# Revit family: MSUi
name_source: partatom
category: Lighting Fixtures
units: mm (PartAtom-declared; Revit-internal decimal feet)

## family parameters
Always vertical = Yes
Cut with Voids When Loaded = No
Host = Ceiling
Light Source = Yes
Maintain Annotation Orientation = No
OmniClass Number = 23.80.70.11.14.17
OmniClass Title = Direct/Indirect
Part Type = Normal
Room Calculation Point = No
Round Connector Dimension = Use Diameter
Shared = No

## types (21) — shared parameters
Assembly Code = D5020200
Default Elevation = 0' - 0"
Description = LED Recessed Medical Surgical with Inset Door Frame
Dimming Lamp Color Temperature Shift = <None>
Emit Shape Visible in Rendering = No
Housing Finish = Metal - Viscor - White
Lamp = LED
Lens Finish = Acrylic - Viscor - Frosted Prismatic P12
Manufacturer = CERTOLUX by VISCOR
Model = MSUi
Tilt Angle = 90.00°
URL = https://www.viscor.com
Voltage = 120 V

## per-type parameters (varying)
| type | Apparent Load | Color Filter | Emit from Rectangle Length | Emit from Rectangle Width | Lamp Wattage | Length | Lens Finish Green | Photometric Web File | Width |
| MSUi-1X4-LED840K035LUNV | 32 VA | 16777215 | 3' - 11 3/4" | 0' - 11 3/4" | 32 VA | 3' - 11 3/4" | Default | MSUi-1X4-LED840K035LUNV.ies | 0' - 11 3/4" |
| MSUi-2X2-LED840K035LUNV | 31 VA | 16777215 | 1' - 11 3/4" | 1' - 11 3/4" | 31 VA | 1' - 11 3/4" | Default | MSUi-2X2-LED840K035LUNV.ies | 1' - 11 3/4" |
| MSUi-2X4-LED840K055LUNV | 45 VA | 16777215 | 3' - 11 3/4" | 1' - 11 3/4" | 45 VA | 3' - 11 3/4" | Default | MSUi-2X4-LED840K055LUNV.ies | 1' - 11 3/4" |
| MSUi-1X4-LED840K055LUNV | 51 VA | 16777215 | 3' - 11 3/4" | 0' - 11 3/4" | 51 VA | 3' - 11 3/4" | Default | MSUi-1X4-LED840K055LUNV.ies | 0' - 11 3/4" |
| MSUi-1X4-LED840K070LUNV | 68 VA | 16777215 | 3' - 11 3/4" | 0' - 11 3/4" | 68 VA | 3' - 11 3/4" | Default | MSUi-1X4-LED840K070LUNV.ies | 0' - 11 3/4" |
| MSUi-1X4-LED840K100LUNV | 96 VA | 16777215 | 3' - 11 3/4" | 0' - 11 3/4" | 96 VA | 3' - 11 3/4" | Default | MSUi-1X4-LED840K100LUNV.ies | 0' - 11 3/4" |
| MSUi-2X2-LED840K055LUNV | 50 VA | 16777215 | 1' - 11 3/4" | 1' - 11 3/4" | 50 VA | 1' - 11 3/4" | Default | MSUi-2X2-LED840K055LUNV.ies | 1' - 11 3/4" |
| MSUi-2X2-LED840K070LUNV | 65 VA | 16777215 | 1' - 11 3/4" | 1' - 11 3/4" | 65 VA | 1' - 11 3/4" | Default | MSUi-2X2-LED840K070LUNV.ies | 1' - 11 3/4" |
| MSUi-2X2-LED840K100LUNV | 93 VA | 16777215 | 1' - 11 3/4" | 1' - 11 3/4" | 93 VA | 1' - 11 3/4" | Default | MSUi-2X2-LED840K100LUNV.ies | 1' - 11 3/4" |
| MSUi-2X4-LED840K070LUNV | 59 VA | 16777215 | 3' - 11 3/4" | 1' - 11 3/4" | 59 VA | 3' - 11 3/4" | <By Category> | MSUi-2X4-LED840K070LUNV.ies | 1' - 11 3/4" |
| MSUi-2X4-LED840K100LUNV | 80 VA | 16777215 | 3' - 11 3/4" | 1' - 11 3/4" | 80 VA | 3' - 11 3/4" | <By Category> | MSUi-2X4-LED840K100LUNV.ies | 1' - 11 3/4" |
| MSUi-2X4-LED840K120LUNV | 99 VA | 16777215 | 3' - 11 3/4" | 1' - 11 3/4" | 99 VA | 3' - 11 3/4" | <By Category> | MSUi-2X4-LED840K120LUNV.ies | 1' - 11 3/4" |
| MSUi-2X4-LED840K180LUNV | 143 VA | 16777215 | 3' - 11 3/4" | 1' - 11 3/4" | 143 VA | 3' - 11 3/4" | <By Category> | MSUi-2X4-LED840K180LUNV.ies | 1' - 11 3/4" |
| MSUi-2X4-LED840K240LUNV | 198 VA | 16777215 | 3' - 11 3/4" | 1' - 11 3/4" | 198 VA | 3' - 11 3/4" | <By Category> | MSUi-2X4-LED840K240LUNV.ies | 1' - 11 3/4" |
| MSUi-1X4-LED840KxxL_32GUNV | 51 VA | 8454016 | 3' - 11 3/4" | 0' - 11 3/4" | 51 VA | 3' - 11 3/4" | Acrylic - Viscor - Frosted Prismatic P12 Green | MSUi-1X4-LED840KxxL_32GUNV.ies | 0' - 11 3/4" |
| MSUi-1X4-LED840KxxL_50GUNV | 80 VA | 8454016 | 3' - 11 3/4" | 0' - 11 3/4" | 80 VA | 3' - 11 3/4" | Acrylic - Viscor - Frosted Prismatic P12 Green | MSUi-1X4-LED840KxxL_50GUNV.ies | 0' - 11 3/4" |
| MSUi-2X2-LED840KxxL_32GUNV | 51 VA | 8454016 | 1' - 11 3/4" | 1' - 11 3/4" | 51 VA | 1' - 11 3/4" | Acrylic - Viscor - Frosted Prismatic P12 Green | MSUi-2X2-LED840KxxL_32GUNV.ies | 1' - 11 3/4" |
| MSUi-2X2-LED840KxxL_50GUNV | 50 VA | 8454016 | 1' - 11 3/4" | 1' - 11 3/4" | 50 VA | 1' - 11 3/4" | Acrylic - Viscor - Frosted Prismatic P12 Green | MSUi-2X2-LED840KxxL_50GUNV.ies | 1' - 11 3/4" |
| MSUi-2X4-LED840KxxL_32GUNV | 45 VA | 8454016 | 3' - 11 3/4" | 1' - 11 3/4" | 45 VA | 3' - 11 3/4" | Acrylic - Viscor - Frosted Prismatic P12 Green | MSUi-2X4-LED840KxxL_32GUNV.ies | 1' - 11 3/4" |
| MSUi-2X4-LED840KxxL_50GUNV | 70 VA | 8454016 | 3' - 11 3/4" | 1' - 11 3/4" | 70 VA | 3' - 11 3/4" | Acrylic - Viscor - Frosted Prismatic P12 Green | MSUi-2X4-LED840KxxL_50GUNV.ies | 1' - 11 3/4" |
| MSUi-2X4-LED840KxxL_100GUNV | 139 VA | 8454016 | 3' - 11 3/4" | 1' - 11 3/4" | 139 VA | 3' - 11 3/4" | Acrylic - Viscor - Frosted Prismatic P12 Green | MSUi-2X4-LED840KxxL_100GUNV.ies | 1' - 11 3/4" |

## geometry (parser evidence)
native form markers: Extrusion x1, Sweep x3
no freeform markers — native parametric forms only
